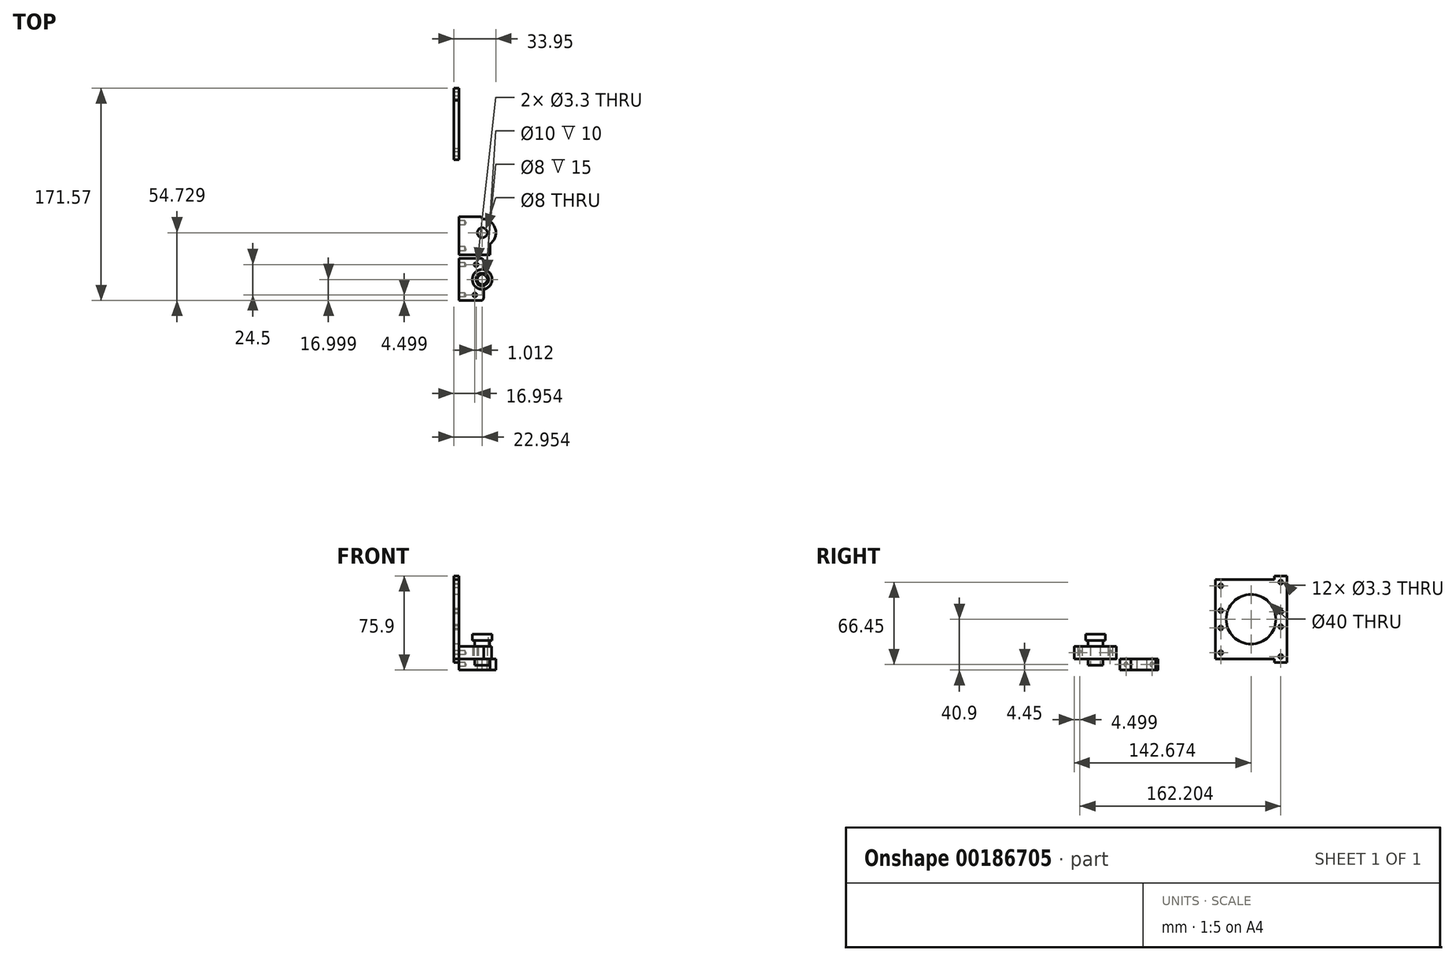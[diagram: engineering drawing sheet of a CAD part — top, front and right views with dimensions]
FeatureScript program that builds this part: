
annotation { "Feature Type Name" : "Feature", "Feature Type Description" : "" }
export const myFeature = defineFeature(function(context is Context, id is Id, definition is map)
    precondition{}
    {
        {
            var Q0;
            Q0=qCreatedBy(makeId("Top.planeOp"),FACE);
            var sketch = newSketch(context, id + "F0", { "sketchPlane" : qUnion([Q0])});
            skLineSegment(sketch, "E0.bottom", {"start": v(20.25, -12.09) * mm, "end": v(54.25, -12.09) * mm});
            skLineSegment(sketch, "E0.top", {"start": v(20.25, -22.09) * mm, "end": v(54.25, -22.09) * mm});
            skLineSegment(sketch, "E0.left", {"start": v(20.25, -12.09) * mm, "end": v(20.25, -22.09) * mm});
            skLineSegment(sketch, "E0.right", {"start": v(54.25, -12.09) * mm, "end": v(54.25, -22.09) * mm});
            skLineSegment(sketch, "E1.bottom", {"start": v(24.23, -61.09) * mm, "end": v(55.23, -61.09) * mm});
            skLineSegment(sketch, "E1.top", {"start": v(24.23, -70.09) * mm, "end": v(55.23, -70.09) * mm});
            skLineSegment(sketch, "E1.left", {"start": v(24.23, -61.09) * mm, "end": v(24.23, -70.09) * mm});
            skLineSegment(sketch, "E1.right", {"start": v(55.23, -61.09) * mm, "end": v(55.23, -70.09) * mm});
            skLineSegment(sketch, "E2.bottom", {"start": v(31.18, -28.09) * mm, "end": v(43.18, -28.09) * mm});
            skLineSegment(sketch, "E2.top", {"start": v(31.18, -7.09) * mm, "end": v(43.18, -7.09) * mm});
            skLineSegment(sketch, "E2.left", {"start": v(31.18, -28.09) * mm, "end": v(31.18, -7.09) * mm});
            skLineSegment(sketch, "E2.right", {"start": v(43.18, -28.09) * mm, "end": v(43.18, -7.09) * mm});
            skLineSegment(sketch, "E3.bottom", {"start": v(46.1, -7.09) * mm, "end": v(28.1, -7.09) * mm});
            skLineSegment(sketch, "E3.top", {"start": v(46.1, -2.09) * mm, "end": v(28.1, -2.09) * mm});
            skLineSegment(sketch, "E3.left", {"start": v(46.1, -7.09) * mm, "end": v(46.1, -2.09) * mm});
            skLineSegment(sketch, "E3.right", {"start": v(28.1, -7.09) * mm, "end": v(28.1, -2.09) * mm});
            skLineSegment(sketch, "E4", {"start": v(37.1, -28.09) * mm, "end": v(37.1, -2.09) * mm, "construction": true});
            skPoint(sketch, "E4.startSnap0", {"position": v(37.1, -2.09) * mm});
            skCircle(sketch, "E5", {"center": v(56.1, -40.38) * mm, "radius": 20 * mm, "construction": true});
            skSolve(sketch);
        }
        {
            var Q0;
            Q0=qCreatedBy(makeId("Top.planeOp"),FACE);
            var sketch = newSketch(context, id + "F1", { "sketchPlane" : qUnion([Q0])});
            skLineSegment(sketch, "E6.bottom", {"start": v(167.7, -150.12) * mm, "end": v(187.7, -150.12) * mm, "construction": true});
            skLineSegment(sketch, "E6.top", {"start": v(167.7, -184.12) * mm, "end": v(187.7, -184.12) * mm, "construction": true});
            skLineSegment(sketch, "E6.left", {"start": v(167.7, -150.12) * mm, "end": v(167.7, -184.12) * mm, "construction": true});
            skLineSegment(sketch, "E6.right", {"start": v(187.7, -150.12) * mm, "end": v(187.7, -184.12) * mm, "construction": true});
            skLineSegment(sketch, "E7", {"start": v(167.7, -167.12) * mm, "end": v(215.44, -167.12) * mm, "construction": true});
            skArc(sketch, "E8", {"start": v(187.7, -174.55) * mm, "mid": v(194.18, -167.12) * mm, "end": v(187.7, -159.69) * mm, "construction": true});
            skPoint(sketch, "E9", {"position": v(180.68, -179.62) * mm});
            skCircle(sketch, "E10.cCircle", {"center": v(186.68, -167.12) * mm, "radius": 5 * mm, "construction": true});
            skLineSegment(sketch, "E10.0", {"start": v(192.46, -167.12) * mm, "end": v(189.57, -172.12) * mm, "construction": true});
            skLineSegment(sketch, "E10.1", {"start": v(189.57, -172.12) * mm, "end": v(183.8, -172.12) * mm, "construction": true});
            skLineSegment(sketch, "E10.2", {"start": v(183.8, -172.12) * mm, "end": v(180.91, -167.12) * mm, "construction": true});
            skLineSegment(sketch, "E10.3", {"start": v(180.91, -167.12) * mm, "end": v(183.8, -162.12) * mm, "construction": true});
            skLineSegment(sketch, "E10.4", {"start": v(183.8, -162.12) * mm, "end": v(189.57, -162.12) * mm, "construction": true});
            skLineSegment(sketch, "E10.5", {"start": v(189.57, -162.12) * mm, "end": v(192.46, -167.12) * mm, "construction": true});
            skPoint(sketch, "E10.0.midPoint", {"position": v(191.01, -169.62) * mm});
            skLineSegment(sketch, "E11", {"start": v(162.94, -149.12) * mm, "end": v(237.76, -149.12) * mm, "construction": true});
            skLineSegment(sketch, "E12.bottom", {"start": v(197.73, -61.35) * mm, "end": v(167.73, -61.35) * mm});
            skLineSegment(sketch, "E12.top", {"start": v(197.73, -70.35) * mm, "end": v(167.73, -70.35) * mm});
            skLineSegment(sketch, "E12.left", {"start": v(197.73, -61.35) * mm, "end": v(197.73, -70.35) * mm});
            skLineSegment(sketch, "E12.right", {"start": v(167.73, -61.35) * mm, "end": v(167.73, -70.35) * mm});
            skLineSegment(sketch, "E13.bottom", {"start": v(167.73, -70.35) * mm, "end": v(163.73, -70.35) * mm});
            skLineSegment(sketch, "E13.top", {"start": v(167.73, -8.35) * mm, "end": v(163.73, -8.35) * mm, "construction": true});
            skLineSegment(sketch, "E13.left", {"start": v(167.73, -70.35) * mm, "end": v(167.73, -12.55) * mm});
            skLineSegment(sketch, "E13.right", {"start": v(163.73, -70.35) * mm, "end": v(163.73, -12.55) * mm});
            skLineSegment(sketch, "E14", {"start": v(167.73, -12.55) * mm, "end": v(220.12, -12.55) * mm, "construction": true});
            skLineSegment(sketch, "E15", {"start": v(182.73, -70.35) * mm, "end": v(186.73, -74.35) * mm, "construction": true});
            skLineSegment(sketch, "E16", {"start": v(186.73, -74.35) * mm, "end": v(190.73, -70.35) * mm, "construction": true});
            skLineSegment(sketch, "E17.top", {"start": v(168.7, -173.12) * mm, "end": v(177.7, -173.12) * mm, "construction": true});
            skLineSegment(sketch, "E17.left", {"start": v(168.7, -167.12) * mm, "end": v(168.7, -173.12) * mm, "construction": true});
            skLineSegment(sketch, "E17.right", {"start": v(177.7, -167.12) * mm, "end": v(177.7, -173.12) * mm, "construction": true});
            skLineSegment(sketch, "E18", {"start": v(168.7, -167.12) * mm, "end": v(168.7, -161.12) * mm, "construction": true});
            skLineSegment(sketch, "E19", {"start": v(168.7, -161.12) * mm, "end": v(177.7, -161.12) * mm, "construction": true});
            skLineSegment(sketch, "E20", {"start": v(177.7, -161.12) * mm, "end": v(177.7, -167.12) * mm, "construction": true});
            skPoint(sketch, "E21", {"position": v(181.7, -155.12) * mm});
            skPoint(sketch, "E22", {"position": v(163.73, -65.85) * mm});
            skPoint(sketch, "E23", {"position": v(163.73, -17.55) * mm});
            skLineSegment(sketch, "E24", {"start": v(167.73, -12.55) * mm, "end": v(163.73, -12.55) * mm});
            skLineSegment(sketch, "E25", {"start": v(167.73, -12.55) * mm, "end": v(167.73, -8.35) * mm, "construction": true});
            skLineSegment(sketch, "E26", {"start": v(163.73, -12.55) * mm, "end": v(163.73, -8.35) * mm, "construction": true});
            skSolve(sketch);
        }
        {
            var Q0;
            Q0=qCreatedBy(makeId("Top.planeOp"),FACE);
            var sketch = newSketch(context, id + "F2", { "sketchPlane" : qUnion([Q0])});
            skPoint(sketch, "E27.0", {"position": v(167.7, -150.12) * mm});
            skPoint(sketch, "E27.1", {"position": v(187.7, -150.12) * mm});
            skPoint(sketch, "E27.2", {"position": v(187.7, -159.69) * mm});
            skPoint(sketch, "E27.3", {"position": v(167.7, -184.12) * mm});
            skPoint(sketch, "E27.4", {"position": v(187.7, -184.12) * mm});
            skPoint(sketch, "E27.5", {"position": v(187.7, -174.55) * mm});
            skPoint(sketch, "E27.6", {"position": v(180.68, -179.62) * mm});
            skLineSegment(sketch, "E28", {"start": v(167.7, -184.12) * mm, "end": v(167.7, -150.12) * mm});
            skLineSegment(sketch, "E29", {"start": v(187.7, -150.12) * mm, "end": v(187.7, -159.69) * mm});
            skLineSegment(sketch, "E30", {"start": v(167.7, -184.12) * mm, "end": v(187.7, -184.12) * mm});
            skLineSegment(sketch, "E31", {"start": v(187.7, -174.55) * mm, "end": v(187.7, -184.12) * mm});
            skPoint(sketch, "E32.0", {"position": v(194.18, -167.12) * mm});
            skLineSegment(sketch, "E33", {"start": v(167.7, -150.12) * mm, "end": v(187.7, -150.12) * mm});
            skArc(sketch, "E34", {"start": v(187.7, -174.55) * mm, "mid": v(194.18, -167.12) * mm, "end": v(187.7, -159.69) * mm});
            skLineSegment(sketch, "E35.0", {"start": v(167.7, -167.12) * mm, "end": v(215.44, -167.12) * mm, "construction": true});
            skSolve(sketch);
        }
        {
            var Q0;
            Q0 = qSketchRegion(id + "F2", true);
            extrude(context, id + "F3", {"entities" : qUnion([Q0]), "depth" : 10 * mm});
        }
        {
            var Q0;
            Q0=makeQuery(id+"F3.opExtrude","SWEPT_EDGE",EDGE,{"disambiguationData":[OSD([sQuery(id+"F2.wireOp",EDGE,"E30"),sQuery(id+"F2.wireOp",EDGE,"E31")])]});
            var Q1;
            Q1=makeQuery(id+"F3.opExtrude","SWEPT_EDGE",EDGE,{"disambiguationData":[OSD([sQuery(id+"F2.wireOp",EDGE,"E29"),sQuery(id+"F2.wireOp",EDGE,"E33")])]});
            fillet(context, id + "F4", {"entities" : qUnion([Q0, Q1]), "radius" : 2 * mm, "tangentPropagation" : true, "allowEdgeOverflow" : false});
        }
        {
            var Q0;
            Q0=makeQuery(id+"F3.opExtrude","SWEPT_EDGE",EDGE,{"disambiguationData":[OSD([sQuery(id+"F2.wireOp",EDGE,"E31"),sQuery(id+"F2.wireOp",EDGE,"E34")])]});
            var Q1;
            Q1=makeQuery(id+"F3.opExtrude","SWEPT_EDGE",EDGE,{"disambiguationData":[OSD([sQuery(id+"F2.wireOp",EDGE,"E29"),sQuery(id+"F2.wireOp",EDGE,"E34")])]});
            fillet(context, id + "F5", {"entities" : qUnion([Q0, Q1]), "radius" : 2 * mm, "tangentPropagation" : true, "allowEdgeOverflow" : false});
        }
        {
            var Q0;
            Q0=makeQuery(id+"F3.opExtrude","CAP_FACE",FACE,{"disambiguationData":[OSD([sQuery(id+"F2.wireOp",EDGE,"E28"),sQuery(id+"F2.wireOp",EDGE,"E29"),sQuery(id+"F2.wireOp",EDGE,"E30"),sQuery(id+"F2.wireOp",EDGE,"E31"),sQuery(id+"F2.wireOp",EDGE,"E33"),sQuery(id+"F2.wireOp",EDGE,"E34")])],"isStart":false});
            var sketch = newSketch(context, id + "F6", { "sketchPlane" : qUnion([Q0])});
            skCircle(sketch, "E36", {"center": v(186.68, -167.12) * mm, "radius": 6 * mm});
            skSolve(sketch);
        }
        {
            var Q0;
            Q0=makeQuery(id+"F6.imprint","IMPRINT",FACE,{"disambiguationData":[TD([[makeQuery(id+"F6.imprint","IMPRINT",EDGE,{"derivedFrom":sQuery(id+"F6.wireOp",EDGE,"E36")}),1.0]])]});
            var Q1;
            Q1=sQuery(id+"F6.wireOp",EDGE,"E36");
            extrude(context, id + "F7", {"entities" : qUnion([Q0]), "operationType" : NewBodyOperationType.ADD, "surfaceEntities" : qUnion([Q1]), "depth" : 5 * mm});
        }
        {
            var Q0;
            Q0=makeQuery(id+"F7.opExtrude","CAP_FACE",FACE,{"disambiguationData":[OSD([sQuery(id+"F6.wireOp",EDGE,"E36")])],"isStart":false});
            var sketch = newSketch(context, id + "F8", { "sketchPlane" : qUnion([Q0])});
            skCircle(sketch, "E37", {"center": v(186.68, -167.12) * mm, "radius": 8 * mm});
            skSolve(sketch);
        }
        {
            var Q0;
            Q0 = qSketchRegion(id + "F8", true);
            extrude(context, id + "F9", {"entities" : qUnion([Q0]), "operationType" : NewBodyOperationType.ADD, "depth" : 5 * mm});
        }
        {
            var Q0;
            Q0=makeQuery(id+"F3.opExtrude","CAP_FACE",FACE,{"disambiguationData":[OSD([sQuery(id+"F2.wireOp",EDGE,"E28"),sQuery(id+"F2.wireOp",EDGE,"E29"),sQuery(id+"F2.wireOp",EDGE,"E30"),sQuery(id+"F2.wireOp",EDGE,"E31"),sQuery(id+"F2.wireOp",EDGE,"E33"),sQuery(id+"F2.wireOp",EDGE,"E34")])],"isStart":true});
            var sketch = newSketch(context, id + "F10", { "sketchPlane" : qUnion([Q0])});
            skCircle(sketch, "E38", {"center": v(186.68, 167.12) * mm, "radius": 6 * mm});
            skSolve(sketch);
        }
        {
            var Q0;
            Q0 = qSketchRegion(id + "F10", true);
            extrude(context, id + "F11", {"entities" : qUnion([Q0]), "operationType" : NewBodyOperationType.ADD, "depth" : 5 * mm});
        }
        {
            var Q0;
            Q0=makeQuery(id+"F9.opExtrude","CAP_FACE",FACE,{"disambiguationData":[OSD([sQuery(id+"F8.wireOp",EDGE,"E37")])],"isStart":false});
            var sketch = newSketch(context, id + "F12", { "sketchPlane" : qUnion([Q0])});
            skCircle(sketch, "E39", {"center": v(186.68, -167.12) * mm, "radius": 5 * mm});
            skSolve(sketch);
        }
        {
            var Q0;
            Q0 = qSketchRegion(id + "F12", true);
            extrude(context, id + "F13", {"entities" : qUnion([Q0]), "operationType" : NewBodyOperationType.REMOVE, "oppositeDirection" : true, "depth" : 10 * mm});
        }
        {
            var Q0;
            Q0=makeQuery(id+"F11.opExtrude","CAP_FACE",FACE,{"disambiguationData":[OSD([sQuery(id+"F10.wireOp",EDGE,"E38")])],"isStart":false});
            var sketch = newSketch(context, id + "F14", { "sketchPlane" : qUnion([Q0])});
            skCircle(sketch, "E40", {"center": v(186.68, 167.12) * mm, "radius": 4 * mm});
            skSolve(sketch);
        }
        {
            var Q0;
            Q0 = qSketchRegion(id + "F14", true);
            var Q1;
            Q1=makeQuery(id+"F9.opExtrude","CAP_FACE",FACE,{"disambiguationData":[OSD([sQuery(id+"F8.wireOp",EDGE,"E37")])],"isStart":false});
            extrude(context, id + "F15", {"entities" : qUnion([Q0]), "operationType" : NewBodyOperationType.REMOVE, "endBound" : BoundingType.UP_TO_SURFACE, "oppositeDirection" : true, "endBoundEntityFace" : qUnion([Q1]), "depth" : 25 * mm});
        }
        {
            var Q0;
            Q0=sQuery(id+"F1.wireOp",VERTEX,"E9");
            var Q1;
            Q1=sQuery(id+"F1.wireOp",VERTEX,"E21");
            var Q2;
            Q2=makeQuery(id+"F3.opExtrude","SWEPT_BODY",BODY,{"disambiguationData":[OSD([sQuery(id+"F2.wireOp",EDGE,"E28"),sQuery(id+"F2.wireOp",EDGE,"E29"),sQuery(id+"F2.wireOp",EDGE,"E30"),sQuery(id+"F2.wireOp",EDGE,"E31"),sQuery(id+"F2.wireOp",EDGE,"E33"),sQuery(id+"F2.wireOp",EDGE,"E34")])]});
            hole(context, id + "F16", {"style" : HoleStyle.SIMPLE, "endStyle" : HoleEndStyle.THROUGH, "oppositeDirection" : true, "standardTappedOrClearance" : lookupTablePath({ "standard" : "ISO", "fit" : "Normal", "size" : "M3", "type" : "Clearance" }), "standardBlindInLast" : lookupTablePath({ "fit" : "Standard", "standard" : "ISO", "size" : "M3", "type" : "Clearance" }), "holeDiameter" : 3.3 * mm, "locations" : qUnion([Q0, Q1]), "scope" : qUnion([Q2]), "isTappedThrough" : true});
        }
        {
            var Q0;
            Q0=makeQuery(id+"F3.opExtrude","SWEPT_FACE",FACE,{"disambiguationData":[OSD([sQuery(id+"F2.wireOp",EDGE,"E28")])]});
            var sketch = newSketch(context, id + "F17", { "sketchPlane" : qUnion([Q0])});
            skLineSegment(sketch, "E41.0", {"start": v(156.77, 10) * mm, "end": v(153.47, 10) * mm, "construction": true});
            skLineSegment(sketch, "E41.1", {"start": v(181.27, 10) * mm, "end": v(177.97, 10) * mm, "construction": true});
            skLineSegment(sketch, "E42", {"start": v(155.12, 10) * mm, "end": v(155.12, 0) * mm, "construction": true});
            skPoint(sketch, "E43", {"position": v(155.12, 5) * mm});
            skLineSegment(sketch, "E44", {"start": v(179.62, 10) * mm, "end": v(179.62, 0) * mm, "construction": true});
            skPoint(sketch, "E45", {"position": v(179.62, 5) * mm});
            skSolve(sketch);
        }
        {
            var Q0;
            Q0=sQuery(id+"F17.wireOp",VERTEX,"E43");
            var Q1;
            Q1=sQuery(id+"F17.wireOp",VERTEX,"E45");
            var Q2;
            Q2=makeQuery(id+"F3.opExtrude","SWEPT_BODY",BODY,{"disambiguationData":[OSD([sQuery(id+"F2.wireOp",EDGE,"E28"),sQuery(id+"F2.wireOp",EDGE,"E29"),sQuery(id+"F2.wireOp",EDGE,"E30"),sQuery(id+"F2.wireOp",EDGE,"E31"),sQuery(id+"F2.wireOp",EDGE,"E33"),sQuery(id+"F2.wireOp",EDGE,"E34")])]});
            hole(context, id + "F18", {"style" : HoleStyle.SIMPLE, "endStyle" : HoleEndStyle.BLIND, "standardTappedOrClearance" : lookupTablePath({ "standard" : "ISO", "fit" : "Normal", "size" : "M3", "type" : "Clearance" }), "standardBlindInLast" : lookupTablePath({ "fit" : "Standard", "standard" : "ISO", "size" : "M3", "type" : "Clearance" }), "holeDiameter" : 3.3 * mm, "holeDepth" : 5 * mm, "locations" : qUnion([Q0, Q1]), "scope" : qUnion([Q2])});
        }
        {
            var Q0;
            Q0=qCreatedBy(makeId("Top.planeOp"),FACE);
            var sketch = newSketch(context, id + "F19", { "sketchPlane" : qUnion([Q0])});
            skLineSegment(sketch, "E46.bottom", {"start": v(167.7, -116.4) * mm, "end": v(186.68, -116.4) * mm});
            skLineSegment(sketch, "E46.top", {"start": v(167.7, -147.4) * mm, "end": v(193, -147.4) * mm});
            skLineSegment(sketch, "E46.left", {"start": v(167.7, -116.4) * mm, "end": v(167.7, -147.4) * mm});
            skLineSegment(sketch, "E46.right", {"start": v(193, -138.4) * mm, "end": v(193, -147.4) * mm});
            skLineSegment(sketch, "E47", {"start": v(186.68, -116.4) * mm, "end": v(186.68, -118.4) * mm});
            skCircle(sketch, "E48.0", {"center": v(186.68, -167.12) * mm, "radius": 5 * mm, "construction": true});
            skLineSegment(sketch, "E49", {"start": v(186.68, -167.12) * mm, "end": v(186.68, -118.4) * mm, "construction": true});
            skLineSegment(sketch, "E50.0", {"start": v(167.7, -150.12) * mm, "end": v(185.7, -150.12) * mm, "construction": true});
            skPoint(sketch, "E51", {"position": v(186.68, -129.4) * mm});
            skArc(sketch, "E52", {"start": v(193, -138.4) * mm, "mid": v(197.17, -126.07) * mm, "end": v(186.68, -118.4) * mm});
            skLineSegment(sketch, "E53", {"start": v(167.7, -150.12) * mm, "end": v(167.7, -147.4) * mm, "construction": true});
            skSolve(sketch);
        }
        {
            var Q0;
            Q0 = qSketchRegion(id + "F19", true);
            extrude(context, id + "F20", {"entities" : qUnion([Q0]), "oppositeDirection" : true, "depth" : 8.9 * mm});
        }
        {
            var Q0;
            Q0=makeQuery(id+"F20.opExtrude","SWEPT_EDGE",EDGE,{"disambiguationData":[OSD([sQuery(id+"F19.wireOp",EDGE,"E46.bottom"),sQuery(id+"F19.wireOp",EDGE,"E47")])]});
            fillet(context, id + "F21", {"entities" : qUnion([Q0]), "radius" : 2 * mm, "tangentPropagation" : true, "allowEdgeOverflow" : false});
        }
        {
            var Q0;
            Q0=sQuery(id+"F19.wireOp",VERTEX,"E51");
            var Q1;
            Q1=makeQuery(id+"F20.opExtrude","SWEPT_BODY",BODY,{"disambiguationData":[OSD([sQuery(id+"F19.wireOp",EDGE,"E46.bottom"),sQuery(id+"F19.wireOp",EDGE,"E46.top"),sQuery(id+"F19.wireOp",EDGE,"E46.left"),sQuery(id+"F19.wireOp",EDGE,"E46.right"),sQuery(id+"F19.wireOp",EDGE,"E47"),sQuery(id+"F19.wireOp",EDGE,"E52")])]});
            hole(context, id + "F22", {"style" : HoleStyle.SIMPLE, "endStyle" : HoleEndStyle.THROUGH, "holeDiameter" : 8 * mm, "locations" : qUnion([Q0]), "scope" : qUnion([Q1]), "isTappedThrough" : true});
        }
        {
            var Q0;
            Q0=makeQuery(id+"F20.opExtrude","SWEPT_FACE",FACE,{"disambiguationData":[OSD([sQuery(id+"F19.wireOp",EDGE,"E46.left")])]});
            var sketch = newSketch(context, id + "F23", { "sketchPlane" : qUnion([Q0])});
            skLineSegment(sketch, "E54", {"start": v(121.4, -8.9) * mm, "end": v(121.4, 0) * mm, "construction": true});
            skLineSegment(sketch, "E55", {"start": v(142.4, -8.9) * mm, "end": v(142.4, 0) * mm, "construction": true});
            skPoint(sketch, "E56", {"position": v(121.4, -4.45) * mm});
            skPoint(sketch, "E57", {"position": v(142.4, -4.45) * mm});
            skSolve(sketch);
        }
        {
            var Q0;
            Q0=sQuery(id+"F23.wireOp",VERTEX,"E56");
            var Q1;
            Q1=sQuery(id+"F23.wireOp",VERTEX,"E57");
            var Q2;
            Q2=makeQuery(id+"F20.opExtrude","SWEPT_BODY",BODY,{"disambiguationData":[OSD([sQuery(id+"F19.wireOp",EDGE,"E46.bottom"),sQuery(id+"F19.wireOp",EDGE,"E46.top"),sQuery(id+"F19.wireOp",EDGE,"E46.left"),sQuery(id+"F19.wireOp",EDGE,"E46.right"),sQuery(id+"F19.wireOp",EDGE,"E47"),sQuery(id+"F19.wireOp",EDGE,"E52")])]});
            hole(context, id + "F24", {"style" : HoleStyle.SIMPLE, "endStyle" : HoleEndStyle.BLIND, "standardTappedOrClearance" : lookupTablePath({ "standard" : "ISO", "fit" : "Normal", "size" : "M3", "type" : "Clearance" }), "standardBlindInLast" : lookupTablePath({ "fit" : "Standard", "standard" : "ISO", "size" : "M3", "type" : "Clearance" }), "holeDiameter" : 3.3 * mm, "holeDepth" : 5 * mm, "locations" : qUnion([Q0, Q1]), "scope" : qUnion([Q2])});
        }
        {
            var Q0;
            {var subQ3=sQuery(id+"F1.wireOp",EDGE,"E13.bottom");Q0=makeQuery(id+"F1.imprint","IMPRINT",FACE,{"disambiguationData":[TD([[makeQuery(id+"F1.imprint","IMPRINT",EDGE,{"derivedFrom":subQ3}),-1.0]])]});}
            extrude(context, id + "F25", {"entities" : qUnion([Q0]), "depth" : 64 * mm});
        }
        {
            var Q0;
            Q0=makeQuery(id+"F25.opExtrude","SWEPT_FACE",FACE,{"disambiguationData":[OSD([sQuery(id+"F1.wireOp",EDGE,"E13.right")])]});
            var sketch = newSketch(context, id + "F26", { "sketchPlane" : qUnion([Q0])});
            skLineSegment(sketch, "E58", {"start": v(41.45, 0) * mm, "end": v(41.45, 64) * mm, "construction": true});
            skLineSegment(sketch, "E59", {"start": v(41.45, 32) * mm, "end": v(70.35, 32) * mm, "construction": true});
            skCircle(sketch, "E60", {"center": v(41.45, 32) * mm, "radius": 20 * mm});
            skSolve(sketch);
        }
        {
            var Q0;
            Q0=makeQuery(id+"F26.imprint","IMPRINT",FACE,{"disambiguationData":[TD([[makeQuery(id+"F26.imprint","IMPRINT",EDGE,{"derivedFrom":sQuery(id+"F26.wireOp",EDGE,"E60")}),1.0]])]});
            var Q1;
            Q1=sQuery(id+"F26.wireOp",EDGE,"E60");
            extrude(context, id + "F27", {"entities" : qUnion([Q0]), "operationType" : NewBodyOperationType.REMOVE, "surfaceEntities" : qUnion([Q1]), "endBound" : BoundingType.THROUGH_ALL, "oppositeDirection" : true, "depth" : 25 * mm});
        }
        {
            var Q0;
            Q0=makeQuery(id+"F25.opExtrude","CAP_FACE",FACE,{"disambiguationData":[OSD([sQuery(id+"F1.wireOp",EDGE,"E13.bottom"),sQuery(id+"F1.wireOp",EDGE,"E13.left"),sQuery(id+"F1.wireOp",EDGE,"E13.right"),sQuery(id+"F1.wireOp",EDGE,"E24")])],"isStart":false});
            var sketch = newSketch(context, id + "F28", { "sketchPlane" : qUnion([Q0])});
            skLineSegment(sketch, "E61.bottom", {"start": v(163.73, -12.55) * mm, "end": v(167.73, -12.55) * mm});
            skLineSegment(sketch, "E61.top", {"start": v(163.73, -22.55) * mm, "end": v(167.73, -22.55) * mm});
            skLineSegment(sketch, "E61.left", {"start": v(163.73, -12.55) * mm, "end": v(163.73, -22.55) * mm});
            skLineSegment(sketch, "E61.right", {"start": v(167.73, -12.55) * mm, "end": v(167.73, -22.55) * mm});
            skSolve(sketch);
        }
        {
            var Q0;
            Q0=makeQuery(id+"F28.imprint","IMPRINT",FACE,{"disambiguationData":[TD([[makeQuery(id+"F28.imprint","IMPRINT",EDGE,{"derivedFrom":sQuery(id+"F28.wireOp",EDGE,"E61.bottom")}),1.0]])]});
            extrude(context, id + "F29", {"entities" : qUnion([Q0]), "operationType" : NewBodyOperationType.ADD, "depth" : 3 * mm});
        }
        {
            var Q0;
            Q0=makeQuery(id+"F25.opExtrude","CAP_FACE",FACE,{"disambiguationData":[OSD([sQuery(id+"F1.wireOp",EDGE,"E13.bottom"),sQuery(id+"F1.wireOp",EDGE,"E13.left"),sQuery(id+"F1.wireOp",EDGE,"E13.right"),sQuery(id+"F1.wireOp",EDGE,"E24")])],"isStart":true});
            var sketch = newSketch(context, id + "F30", { "sketchPlane" : qUnion([Q0])});
            skLineSegment(sketch, "E62.bottom", {"start": v(167.73, 12.55) * mm, "end": v(163.73, 12.55) * mm});
            skLineSegment(sketch, "E62.top", {"start": v(167.73, 22.55) * mm, "end": v(163.73, 22.55) * mm});
            skLineSegment(sketch, "E62.left", {"start": v(167.73, 12.55) * mm, "end": v(167.73, 22.55) * mm});
            skLineSegment(sketch, "E62.right", {"start": v(163.73, 12.55) * mm, "end": v(163.73, 22.55) * mm});
            skSolve(sketch);
        }
        {
            var Q0;
            Q0=makeQuery(id+"F30.imprint","IMPRINT",FACE,{"disambiguationData":[TD([[makeQuery(id+"F30.imprint","IMPRINT",EDGE,{"derivedFrom":sQuery(id+"F30.wireOp",EDGE,"E62.bottom")}),-1.0]])]});
            extrude(context, id + "F31", {"entities" : qUnion([Q0]), "operationType" : NewBodyOperationType.ADD, "depth" : 3 * mm});
        }
        {
            var Q0;
            Q0=makeQuery(id+"F25.opExtrude","SWEPT_FACE",FACE,{"disambiguationData":[OSD([sQuery(id+"F1.wireOp",EDGE,"E13.right")])]});
            var sketch = newSketch(context, id + "F32", { "sketchPlane" : qUnion([Q0])});
            skLineSegment(sketch, "E63", {"start": v(17.42, 0) * mm, "end": v(17.42, 64) * mm, "construction": true});
            skLineSegment(sketch, "E64", {"start": v(65.84, 0) * mm, "end": v(65.84, 64) * mm, "construction": true});
            skPoint(sketch, "E65", {"position": v(17.42, 2) * mm});
            skPoint(sketch, "E66", {"position": v(17.42, 62) * mm});
            skPoint(sketch, "E67", {"position": v(65.84, 5) * mm});
            skPoint(sketch, "E68", {"position": v(65.84, 59) * mm});
            skPoint(sketch, "E69", {"position": v(17.42, 26) * mm});
            skPoint(sketch, "E70", {"position": v(17.42, 38) * mm});
            skPoint(sketch, "E71", {"position": v(17.42, 32) * mm});
            skPoint(sketch, "E72", {"position": v(65.84, 32) * mm});
            skPoint(sketch, "E73", {"position": v(65.84, 25) * mm});
            skPoint(sketch, "E74", {"position": v(65.84, 39) * mm});
            skSolve(sketch);
        }
        {
            var Q0;
            Q0=sQuery(id+"F32.wireOp",VERTEX,"E65");
            var Q1;
            Q1=sQuery(id+"F32.wireOp",VERTEX,"E66");
            var Q2;
            Q2=sQuery(id+"F32.wireOp",VERTEX,"E68");
            var Q3;
            Q3=sQuery(id+"F32.wireOp",VERTEX,"E67");
            var Q4;
            Q4=sQuery(id+"F32.wireOp",VERTEX,"E69");
            var Q5;
            Q5=sQuery(id+"F32.wireOp",VERTEX,"E70");
            var Q6;
            Q6=sQuery(id+"F32.wireOp",VERTEX,"E73");
            var Q7;
            Q7=sQuery(id+"F32.wireOp",VERTEX,"E74");
            var Q8;
            Q8=makeQuery(id+"F25.opExtrude","SWEPT_BODY",BODY,{"disambiguationData":[OSD([sQuery(id+"F1.wireOp",EDGE,"E13.bottom"),sQuery(id+"F1.wireOp",EDGE,"E13.top"),sQuery(id+"F1.wireOp",EDGE,"E13.left"),sQuery(id+"F1.wireOp",EDGE,"E13.right")])]});
            hole(context, id + "F33", {"style" : HoleStyle.SIMPLE, "endStyle" : HoleEndStyle.BLIND, "standardTappedOrClearance" : lookupTablePath({ "standard" : "ISO", "fit" : "Normal", "size" : "M3", "type" : "Clearance" }), "standardBlindInLast" : lookupTablePath({ "fit" : "Standard", "standard" : "ISO", "size" : "M3", "type" : "Clearance" }), "holeDiameter" : 3.3 * mm, "holeDepth" : 5 * mm, "locations" : qUnion([Q0, Q1, Q2, Q3, Q4, Q5, Q6, Q7]), "scope" : qUnion([Q8])});
        }
    });
